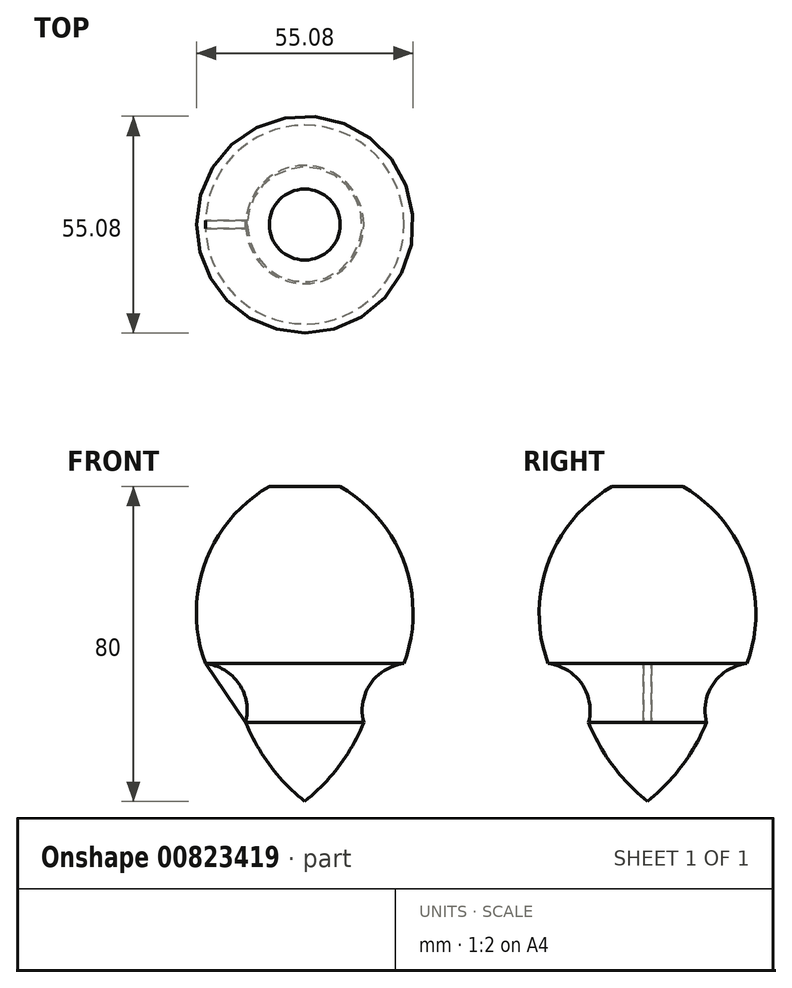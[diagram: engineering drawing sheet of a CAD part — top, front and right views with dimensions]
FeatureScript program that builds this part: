
annotation { "Feature Type Name" : "Feature", "Feature Type Description" : "" }
export const myFeature = defineFeature(function(context is Context, id is Id, definition is map)
    precondition{}
    {
        {
            var Q0;
            Q0=qCreatedBy(makeId("Front.planeOp"),FACE);
            var sketch = newSketch(context, id + "F0", { "sketchPlane" : qUnion([Q0])});
            skLineSegment(sketch, "E0", {"start": v(0, 0) * mm, "end": v(0, 80) * mm});
            skLineSegment(sketch, "E1", {"start": v(0, 80) * mm, "end": v(9, 80) * mm});
            skLineSegment(sketch, "E2", {"start": v(0, 20) * mm, "end": v(15, 20) * mm});
            skLineSegment(sketch, "E3", {"start": v(0, 35) * mm, "end": v(25.25, 35) * mm});
            skArc(sketch, "E4", {"start": v(25.25, 35) * mm, "mid": v(25.33, 60.46) * mm, "end": v(9, 80) * mm});
            skArc(sketch, "E5", {"start": v(25.25, 35) * mm, "mid": v(16.7, 29.85) * mm, "end": v(15, 20) * mm});
            skArc(sketch, "E6", {"start": v(0, 0) * mm, "mid": v(8.77, 9.05) * mm, "end": v(15, 20) * mm});
            skSolve(sketch);
        }
        {
            var Q0;
            {var subQ0=sQuery(id+"F0.wireOp",EDGE,"E2");Q0=makeQuery(id+"F0.imprint","IMPRINT",FACE,{"disambiguationData":[TD([[makeQuery(id+"F0.imprint","IMPRINT",EDGE,{"derivedFrom":subQ0}),1.0]])]});}
            var Q1;
            {var subQ2=sQuery(id+"F0.wireOp",EDGE,"E2");Q1=makeQuery(id+"F0.imprint","IMPRINT",FACE,{"disambiguationData":[TD([[makeQuery(id+"F0.imprint","IMPRINT",EDGE,{"derivedFrom":subQ2}),-1.0]])]});}
            var Q2;
            {var subQ0=sQuery(id+"F0.wireOp",EDGE,"E1");Q2=makeQuery(id+"F0.imprint","IMPRINT",FACE,{"disambiguationData":[TD([[makeQuery(id+"F0.imprint","IMPRINT",EDGE,{"derivedFrom":subQ0}),-1.0]])]});}
            var Q3;
            Q3=sQuery(id+"F0.wireOp",EDGE,"E0");
            revolve(context, id + "F1", {"surfaceOperationType" : NewSurfaceOperationType.NEW, "entities" : qUnion([Q0, Q1, Q2]), "axis" : qUnion([Q3]), "revolveType" : RevolveType.FULL});
        }
        {
            var Q0;
            Q0=qCreatedBy(makeId("Front.planeOp"),FACE);
            var sketch = newSketch(context, id + "F2", { "sketchPlane" : qUnion([Q0])});
            skArc(sketch, "E7", {"start": v(-15, 20) * mm, "mid": v(-16.7, 29.85) * mm, "end": v(-25.25, 35) * mm});
            skLineSegment(sketch, "E8", {"start": v(-25.25, 35) * mm, "end": v(-15, 20) * mm});
            skSolve(sketch);
        }
        {
            var Q0;
            Q0 = qSketchRegion(id + "F2", true);
            extrude(context, id + "F3", {"entities" : qUnion([Q0]), "operationType" : NewBodyOperationType.ADD, "endBound" : BoundingType.SYMMETRIC, "depth" : 2 * mm, "offsetDistance" : 25 * mm});
        }
    });
